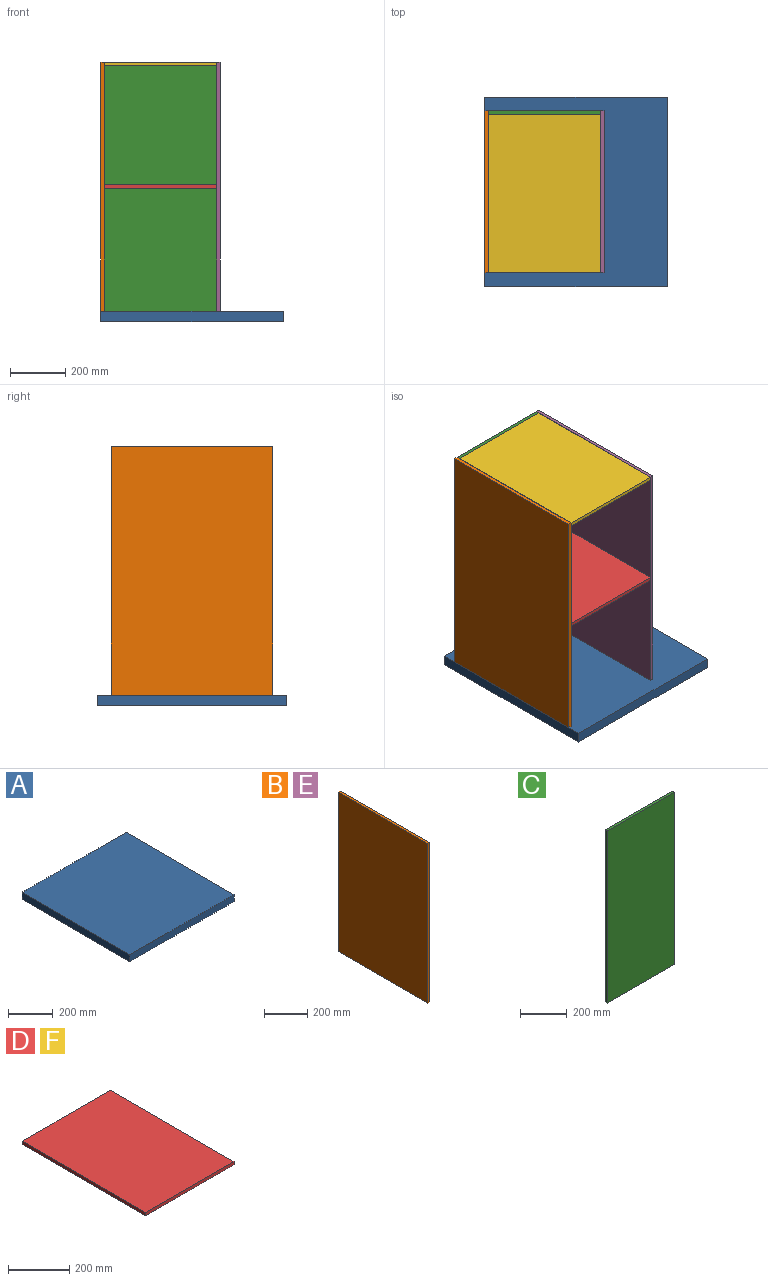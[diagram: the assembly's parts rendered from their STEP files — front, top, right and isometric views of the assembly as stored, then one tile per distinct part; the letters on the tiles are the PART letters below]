
ASSEMBLY  parts=6 mates=5
PART A: 6 faces, bbox 660.4x685.8x38.1 mm
  f0: plane 685.8x38.1mm, normal (1,0,0), area 26129mm2, adj f1,f3,f4,f5
  f1: plane 660.4x38.1mm, normal (0,1,0), area 25161.2mm2, adj f0,f2,f4,f5
  f2: plane 685.8x38.1mm, normal (-1,0,0), area 26129mm2, adj f1,f3,f4,f5
  f3: plane 660.4x38.1mm, normal (0,-1,0), area 25161.2mm2, adj f0,f2,f4,f5
  f4: plane 685.8x660.4mm, normal (0,0,1), area 452902.3mm2, adj f0,f1,f2,f3
  f5: plane 685.8x660.4mm, normal (0,0,-1), area 452902.3mm2, adj f0,f1,f2,f3
PART B: 6 faces, bbox 12.7x584.2x901.7 mm
  f0: plane 901.7x12.7mm, normal (0,1,0), area 11451.6mm2, adj f1,f3,f4,f5
  f1: plane 584.2x12.7mm, normal (0,0,1), area 7419.3mm2, adj f0,f2,f4,f5
  f2: plane 901.7x12.7mm, normal (0,-1,0), area 11451.6mm2, adj f1,f3,f4,f5
  f3: plane 584.2x12.7mm, normal (0,0,-1), area 7419.3mm2, adj f0,f2,f4,f5
  f4: plane 901.7x584.2mm, normal (1,0,0), area 526773.1mm2, adj f0,f1,f2,f3
  f5: plane 901.7x584.2mm, normal (-1,0,0), area 526773.1mm2, adj f0,f1,f2,f3
PART C: 6 faces, bbox 406.4x12.7x901.7 mm
  f0: plane 406.4x12.7mm, normal (0,0,-1), area 5161.3mm2, adj f1,f3,f4,f5
  f1: plane 901.7x12.7mm, normal (1,0,0), area 11451.6mm2, adj f0,f2,f4,f5
  f2: plane 406.4x12.7mm, normal (0,0,1), area 5161.3mm2, adj f1,f3,f4,f5
  f3: plane 901.7x12.7mm, normal (-1,0,0), area 11451.6mm2, adj f0,f2,f4,f5
  f4: plane 901.7x406.4mm, normal (0,-1,0), area 366450.9mm2, adj f0,f1,f2,f3
  f5: plane 901.7x406.4mm, normal (0,1,0), area 366450.9mm2, adj f0,f1,f2,f3
PART D: 6 faces, bbox 406.4x571.5x12.7 mm
  f0: plane 571.5x12.7mm, normal (1,0,0), area 7258mm2, adj f1,f3,f4,f5
  f1: plane 406.4x12.7mm, normal (0,1,0), area 5161.3mm2, adj f0,f2,f4,f5
  f2: plane 571.5x12.7mm, normal (-1,0,0), area 7258mm2, adj f1,f3,f4,f5
  f3: plane 406.4x12.7mm, normal (0,-1,0), area 5161.3mm2, adj f0,f2,f4,f5
  f4: plane 571.5x406.4mm, normal (0,0,1), area 232257.6mm2, adj f0,f1,f2,f3
  f5: plane 571.5x406.4mm, normal (0,0,-1), area 232257.6mm2, adj f0,f1,f2,f3
PART E: same geometry as B
PART F: same geometry as D
PLACE A t=(114.3,-292.1,-488.95)mm
PLACE B rot(axis=(0,1,0),180deg) t=(-203.2,-292.1,0)mm
PLACE C at identity fixed
PLACE D rot(axis=(1,0,0),180deg) t=(0,-298.45,6.35)mm
PLACE E rot(axis=(-1,0,0),180deg) t=(203.2,-292.1,0)mm
PLACE F rot(axis=(1,0,0),180deg) t=(0,-298.45,450.85)mm
MATE fastened C.f4 <-> F.f3  axis (0,-1,0) through (0,-12.7,450.85)mm
MATE fastened B.f0 <-> C.f5  axis (0,1,0) through (-209.55,0,0)mm
MATE fastened E.f2 <-> C.f5  axis (0,1,0) through (209.55,0,0)mm
MATE fastened C.f4 <-> D.f3  axis (0,-1,0) through (0,-12.7,0)mm
MATE fastened B.f1 <-> A.f4  axis (0,0,-1) through (-209.55,-292.1,-450.85)mm
